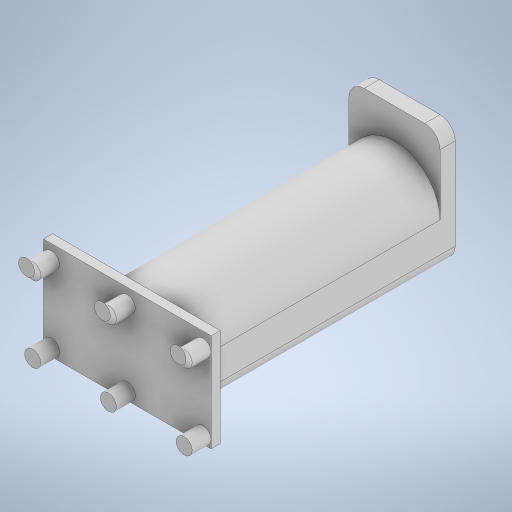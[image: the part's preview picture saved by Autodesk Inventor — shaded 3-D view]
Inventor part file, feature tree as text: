
AUTODESK INVENTOR PART (.ipt)
format: ipt  version: 2024 (Build 280153000, 153)  size: 410,624 bytes
history: native  units: mm
features: other x10, sketch x7, extrude x6, fillet x4, pattern_linear x3, chamfer x2, loft x1
ambient origin geometry x8: Origin, YZ Plane, XZ Plane, XY Plane, X Axis, Y Axis, Z Axis, Center Point
bodies: Body1 (feature_tree)
feature tree (33):
  other  "Твердое тело1"
  extrude  "Выдавливание1"  Depth=1.85mm TaperAngle=0.0deg
  extrude  "Выдавливание2"  Depth=55.2mm
  pattern_linear  "Прямоуг.массив1"  Spacing1=32.25mm  [1 undecoded]
  extrude  "Выдавливание3"  Depth=5.3mm
  extrude  "Выдавливание4"  Depth=6.2mm TaperAngle=0.0deg
  fillet  "Сопряжение1"  Radius=20.0mm
  pattern_linear  "Прямоуг.массив2"  Spacing1=24.95mm  [1 undecoded]
  fillet  "Сопряжение2"  Radius=31.1875mm
  other  "РабПлоскость1"
  loft  "Лофт1"
  pattern_linear  "Прямоуг.массив3"  Spacing1=35.0mm  [1 undecoded]
  other  "Удаление грани1"
  other  "Непосредственное редактирование1"
  extrude  "Выдавливание6"  Depth=29.1875mm
  extrude  "Выдавливание7"  TaperAngle=0.0deg  [1 undecoded]
  fillet  "Сопряжение3"  Radius=10.0mm
  other  "Непосредственное редактирование2"
  other  "Удаление грани2"
  fillet  "Сопряжение4"  Radius=2.0mm
  chamfer  "Фаска1"  Distance=10.0mm
  chamfer  "Фаска2"  Distance=10.0mm
  sketch  "Эскиз1"
  sketch  "Эскиз2"
  sketch  "Эскиз3"
  sketch  "Эскиз4"
  sketch  "Эскиз7"
  other  "Ребра1"
  sketch  "Эскиз10"
  sketch  "Эскиз11"
  other  "Перенос1"
  other  "Перенос2"
  other  "Перенос3"
note: 4 required parameter values undecoded (feature->parameter linkage not recoverable at this tier; creation-order binding heuristic only, values carry confidence <= 0.55)
